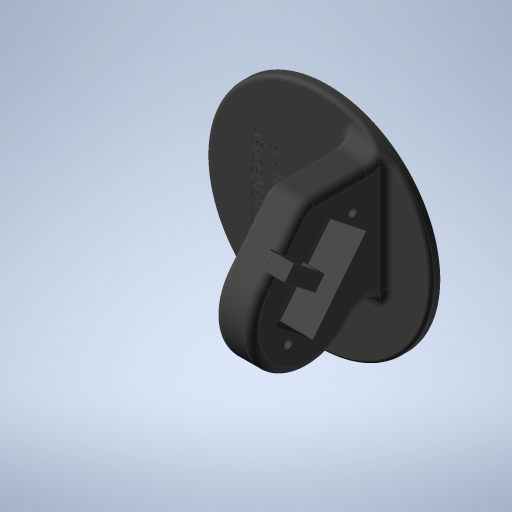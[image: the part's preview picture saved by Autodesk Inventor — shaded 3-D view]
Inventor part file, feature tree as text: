
AUTODESK INVENTOR PART (.ipt)
format: ipt  version: 2023.2 (Build 272271000, 271)  size: 810,496 bytes
history: native  units: mm
features: sketch x9, extrude x5, fillet x5, hole x3, emboss x1, plane x1
ambient origin geometry x8: Origin, YZ Plane, XZ Plane, XY Plane, X Axis, Y Axis, Z Axis, Center Point
bodies: Solid1 (feature_tree)
feature tree (24):
  extrude  "Extrusion1"  Depth=2.5mm TaperAngle=0.0deg
  hole  "Hole1"  [1 undecoded]
  hole  "Hole2"  [1 undecoded]
  emboss  "Emboss1"
  plane  "Work Plane1"
  extrude  "Extrusion2"  Depth=6.1mm
  extrude  "Extrusion5"  Depth=10.0mm
  hole  "Hole4"  [1 undecoded]
  fillet  "Fillet1"  Radius=10.0mm
  fillet  "Fillet2"  Radius=2.5mm
  fillet  "Fillet3"  Radius=8.7mm
  fillet  "Fillet4"  Radius=27.8mm
  extrude  "Extrusion6"  Depth=5.0mm
  fillet  "Fillet5"  Radius=2.0mm
  extrude  "Extrusion7"  Depth=2.0mm
  sketch  "Sketch1"  dims[d0=60.0mm d1=2.5mm d2=0.0mm]
  sketch  "Sketch2"  dims[d3=17.0mm]
  sketch  "Sketch3"  dims[d4=2.1mm d5=6.0mm d6=4.0mm d7=2.0mm d8=90.0deg d9=8.0mm d10=0.0mm]
  sketch  "Sketch4"  dims[d11=8.0mm d12=6.0mm d13=4.0mm d14=2.0mm d15=90.0deg d16=8.0mm d17=0.0mm d18=1.0mm d19=0.0mm]
  sketch  "Sketch5"  dims[d20=8.0mm d21=12.6mm]
  sketch  "Sketch10"  dims[d22=22.6mm d23=6.1mm]
  sketch  "Sketch11"  dims[d24=10.0mm d25=32.4mm]
  sketch  "Sketch12"  dims[d26=2.5mm d27=2.5mm d28=10.0mm d29=0.0mm d64=2.5mm]
  sketch  "Sketch13"  dims[d66=13.0mm d67=23.0mm d68=6.3mm d69=10.0mm d70=32.4mm d71=2.5mm d72=2.5mm d73=2.5mm d74=8.7mm d75=0.0mm d76=27.8mm d77=2.0mm d78=6.0mm d79=4.0mm d80=2.0mm d81=90.0deg d82=7.0mm d83=0.0mm d84=5.0mm d85=2.0mm d86=2.0mm d87=1.0mm d88=9.5mm d89=1.0mm d90=5.0mm d91=0.0mm d92=2.0mm d93=1.0mm d94=1.0mm d95=2.5mm d96=0.0mm d97=2.0mm d98=1.0mm d99=1.0mm d100=1.0mm d101=5.0mm d102=0.0mm]
note: 3 required parameter values undecoded (feature->parameter linkage not recoverable at this tier; creation-order binding heuristic only, values carry confidence <= 0.55)
